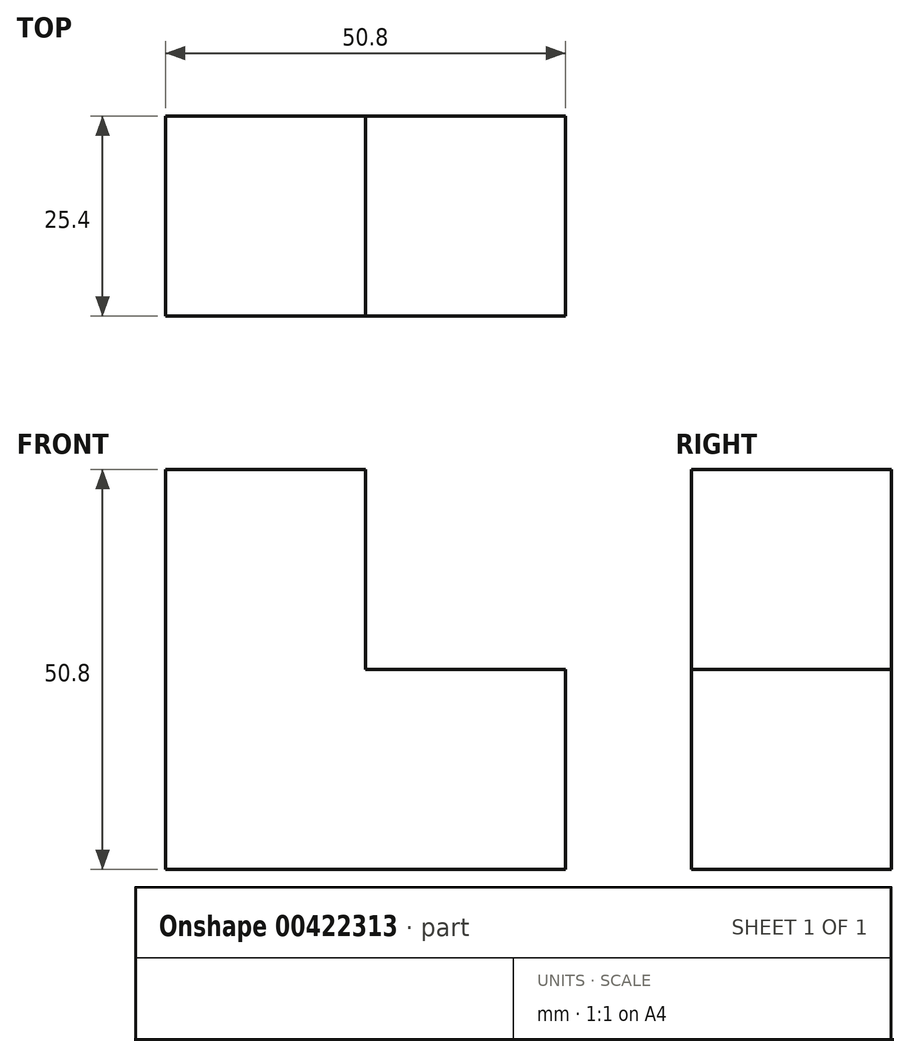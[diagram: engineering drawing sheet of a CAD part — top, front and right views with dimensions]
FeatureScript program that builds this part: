
annotation { "Feature Type Name" : "Feature", "Feature Type Description" : "" }
export const myFeature = defineFeature(function(context is Context, id is Id, definition is map)
    precondition{}
    {
        {
            var Q0;
            Q0=qCreatedBy(makeId("Front.planeOp"),FACE);
            var sketch = newSketch(context, id + "F0", { "sketchPlane" : qUnion([Q0])});
            skLineSegment(sketch, "E0", {"start": v(-53.34, 9.38) * mm, "end": v(-53.34, -41.42) * mm});
            skLineSegment(sketch, "E1", {"start": v(-53.34, -41.42) * mm, "end": v(-2.54, -41.42) * mm});
            skLineSegment(sketch, "E2", {"start": v(-53.34, 9.38) * mm, "end": v(-27.94, 9.38) * mm});
            skLineSegment(sketch, "E3", {"start": v(-27.94, 9.38) * mm, "end": v(-27.94, -16.02) * mm});
            skLineSegment(sketch, "E4", {"start": v(-27.94, -16.02) * mm, "end": v(-2.54, -16.02) * mm});
            skLineSegment(sketch, "E5", {"start": v(-2.54, -16.02) * mm, "end": v(-2.54, -41.42) * mm});
            skSolve(sketch);
        }
        {
            var Q0;
            Q0 = qSketchRegion(id + "F0", true);
            extrude(context, id + "F1", {"entities" : qUnion([Q0]), "depth" : 25.4 * mm});
        }
    });
